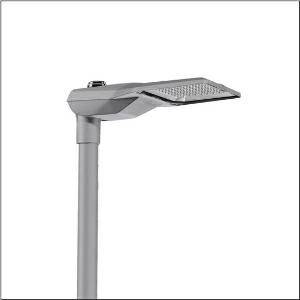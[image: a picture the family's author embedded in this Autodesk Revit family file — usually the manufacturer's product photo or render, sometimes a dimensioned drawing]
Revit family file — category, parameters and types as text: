
# Revit family: streetlight_sl_21_midi___st0_5a_5xe7b37n08lb_6898
name_source: partatom
category: Lighting Fixtures
units: mm (PartAtom-declared; Revit-internal decimal feet)

## family parameters
Cut with Voids When Loaded = No
Host = Face
Light Source = No
Part Type = Normal
Room Calculation Point = No
Round Connector Dimension = Use Diameter
Shared = No

## types (1)
- --- (1 x LED, 14340 lm, 98.3 W, 3000K)
    Apparent Load = 98 VA
    CIE Flux Codes = 41 75 97 100 100
    Color Rendering = 70
    Color Temperature = 3000K
    Default Elevation = 1800 mm
    Description = Streetlight SL 21 midi, mast luminaire, primary light control with lens, of PMMA, primary optical cover: cover, of toughened safety glass, transparent, light distribution: ST0.5a, light emission: direct distribution, primary light characteristic: asymmetric, installation type: side-entry, LED, 3G 2.5mm², High Power LED, rated luminous flux: 14.340lm, luminous efficacy: 146lm/W, light colour: 730, colour temperature: 3000K, control gear: NEMA (7pin), control: overheat protection, pre-setting: linear dimming characteristic, constant luminous flux control, time-dependent luminous flux control, flexible luminous flux parameterisation, mains connection: 220..240V, AC, 50/60Hz, connection cable pre-assembled, cable length: 10,5m, wiring characteristics: H05VV-F, start of lifetime: 98W, end of service life: 101W, reduction: 45W, luminaire housing, of diecast aluminium (EN AC-44300), powder-coated, Siteco® metallic grey (DB 702S), corrosivity category C5 mid according to DIN EN ISO 12944, multi-level sealing system, sealing non-destructively replaceable, inclination adjustable: 0°, 5°, 10°, 15°, length: 644mm, width: 335mm, height: 110mm, spigot size: 42mm (side-entry), mounting height: 4..8m, protection rating (complete): IP66, insulation class (complete): insulation class I (protective earthing), certification: CE, ENEC, ENEC+, VDE, impact resistance: IK09, permissible operating ambient temperature for outdoor applications: -40..+50°C, standard-compliant lighting for roads and squares, packaging unit: 1 piece

Light Distribution: ST0.5a
    Height = 111 mm
    Lamp = 1 x LED
    Lamp Light Flux = 14340 lm
    Lamp Power = 98.3 W
    Lamp count = 1
    Length = 644 mm
    Luminous efficacy = 146 lm/W
    Manufacturer = Siteco
    ModVariant = No
    Model = 5XE7B37N08LB
    Number of Poles = 1
    OnlyDefault = Yes
    Power Factor = 1
    Product Name = Streetlight SL 21 midi | ST0.5a
    Product group = mast luminaire | pylon top
    ProductGroupID = 6100
    Protection Class = Protection class I
    Protection Degree = IP 66
    RLX_Detail_Level = 1
    RLX_Emergency_Light_Flux = 0 lm
    RLX_Emergency_Type = 0
    RLX_Emergency_Type_DB = No
    RlxData = <blob elided: 101565 chars, md5=95ed8842>
    Socket = socket
    Standby Power = 0 W
    System Light Flux = 14340 lm
    System Power = 98 W
    Type Comments = factory setting: luminous flux: 100 % | dim-lin: 254 | 1020 mA
    Type Image = l_1294377.jpg
    URL = http://relux.com
    VarID = @adj_132684
    Voltage = 0 V
    Weight = 0.00 kg
    Width = 336 mm

## geometry (parser evidence)
native form markers: Blend x4, Sweep x9
no freeform markers — native parametric forms only
